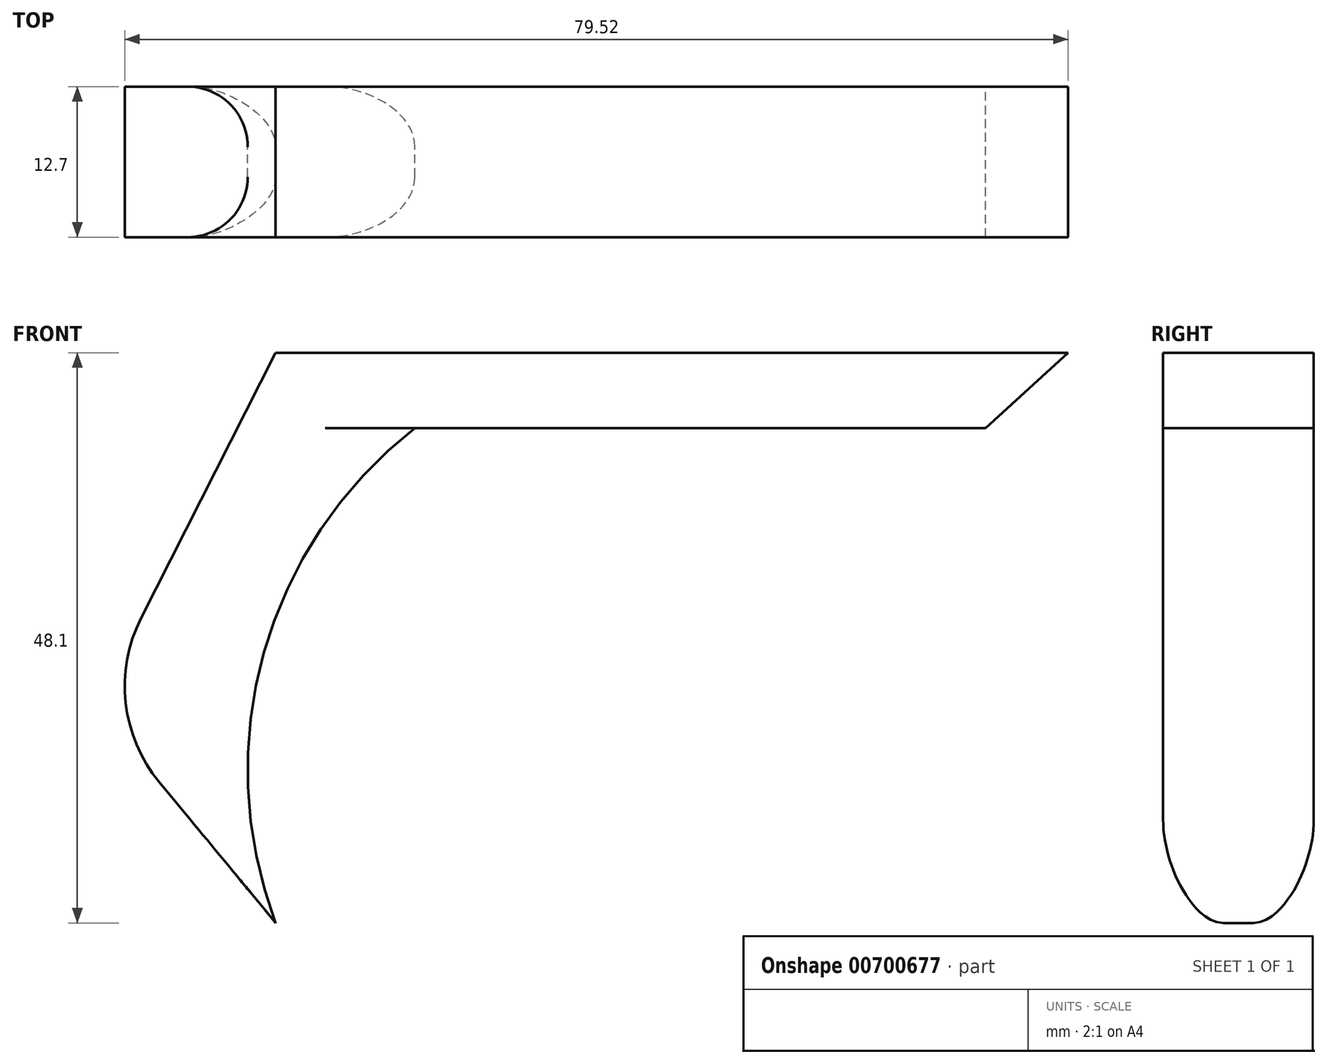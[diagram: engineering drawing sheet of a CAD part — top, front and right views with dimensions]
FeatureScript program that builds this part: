
annotation { "Feature Type Name" : "Feature", "Feature Type Description" : "" }
export const myFeature = defineFeature(function(context is Context, id is Id, definition is map)
    precondition{}
    {
        {
            var Q0;
            Q0=qCreatedBy(makeId("Front.planeOp"),FACE);
            var sketch = newSketch(context, id + "F0", { "sketchPlane" : qUnion([Q0])});
            skLineSegment(sketch, "E0", {"start": v(0, 0) * mm, "end": v(66.8, 0) * mm});
            skLineSegment(sketch, "E1", {"start": v(66.8, 0) * mm, "end": v(59.84, -6.35) * mm});
            skLineSegment(sketch, "E2", {"start": v(59.84, -6.35) * mm, "end": v(11.75, -6.35) * mm});
            skLineSegment(sketch, "E3", {"start": v(0, 0) * mm, "end": v(-11.34, -22.38) * mm});
            skLineSegment(sketch, "E4", {"start": v(-9.81, -36.2) * mm, "end": v(0, -48.1) * mm});
            skArc(sketch, "E5", {"start": v(11.75, -6.35) * mm, "mid": v(-0.98, -25.3) * mm, "end": v(0, -48.1) * mm});
            skPoint(sketch, "E6.visualSharp", {"position": v(-15.1, -29.8) * mm});
            skArc(sketch, "E6.filletArc", {"start": v(-11.34, -22.38) * mm, "mid": v(-12.64, -29.53) * mm, "end": v(-9.81, -36.2) * mm});
            skSolve(sketch);
        }
        {
            var Q0;
            Q0 = qSketchRegion(id + "F0", true);
            extrude(context, id + "F1", {"entities" : qUnion([Q0]), "depth" : 12.7 * mm, "offsetDistance" : 25.4 * mm});
        }
        {
            var Q0;
            Q0=makeQuery(id+"F1.opExtrude","CAP_EDGE",EDGE,{"disambiguationData":[OSD([sQuery(id+"F0.wireOp",EDGE,"E5")])],"isStart":false});
            var Q1;
            Q1=makeQuery(id+"F1.opExtrude","CAP_EDGE",EDGE,{"disambiguationData":[OSD([sQuery(id+"F0.wireOp",EDGE,"E5")])],"isStart":true});
            fillet(context, id + "F2", {"entities" : qUnion([Q0, Q1]), "radius" : 5.08 * mm, "tangentPropagation" : true, "allowEdgeOverflow" : false});
        }
    });
